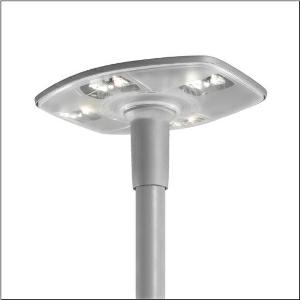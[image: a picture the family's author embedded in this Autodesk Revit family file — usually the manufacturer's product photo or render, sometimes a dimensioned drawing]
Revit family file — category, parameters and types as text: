
# Revit family: dl_30_led___st1_2c_5xa513281b08a5_8ddb
name_source: partatom
category: Lighting Fixtures
units: mm (PartAtom-declared; Revit-internal decimal feet)

## family parameters
Cut with Voids When Loaded = No
Host = Face
Light Source = No
Part Type = Normal
Room Calculation Point = No
Round Connector Dimension = Use Diameter
Shared = No

## types (1)
- --- (1 x LED, 4590 lm, 49 W, 3000K)
    Apparent Load = 49 VA
    CIE Flux Codes = 32 71 98 100 100
    Color Rendering = 80
    Color Temperature = 3000K
    Default Elevation = 1800 mm
    Description = DL 30 LED, mast luminaire, primary light control with 3 zone facetted reflector, of plastic, aluminium vaporised, highly specular, primary optical cover: cover, of PMMA, structured, transparent, light distribution: ST1.2c, light emission: direct distribution, primary light characteristic: asymmetric, crossroads, installation type: post-top, LED, High Power LED, rated luminous flux: 4.590lm, luminous efficacy: 94lm/W, light colour: 830, colour temperature: 3000K, control gear: Plus, control: flexible luminous flux parameterisation, time-dependent luminous flux control, constant luminous flux control, digital communication interface, power reduction, electronic power reduction, mains connection: 230..240V, AC, 50/60Hz, start of lifetime: 49W, end of service life: 51W, reduction: 22W, luminaire housing, of diecast aluminium, powder-coated, SITECO metallic grey (DB 702S), length: 600mm, width: 510mm, height: 290mm, spigot size: d x l = 76 x 100mm (post-top) | with reducer (optional accessory) 60 x 100mm, mounting height: 3..6m, protection rating (complete): IP66, insulation class (complete): insulation class II (safety insulation), certification: CE, ENEC, VDE, impact resistance: IK08, permissible operating ambient temperature: -25..+30°C, standard-compliant lighting for roads and squares, packaging unit: 1 piece

Light Distribution: ST1.2c
    Height = 290 mm
    Lamp = 1 x LED
    Lamp Light Flux = 4590 lm
    Lamp Power = 49 W
    Lamp count = 1
    Length = 510 mm
    Luminous efficacy = 94 lm/W
    Manufacturer = Siteco
    ModVariant = No
    Model = 5XA513281B08A5
    Mounting Place = Pole
    Mounting Type = Pole top
    Number of Poles = 1
    OnlyDefault = Yes
    Power Factor = 1
    Product Name = DL 30 LED | ST1.2c
    Product group = mast luminaire | pylon top
    ProductGroupID = 6100
    Protection Class = Protection class II
    Protection Degree = IP 66
    RLX_Detail_Level = 1
    RLX_Emergency_Light_Flux = 0 lm
    RLX_Emergency_Type = 0
    RLX_Emergency_Type_DB = No
    RlxData = <blob elided: 86557 chars, md5=80c81cf2>
    Socket = socket
    Standby Power = 0 W
    System Light Flux = 4590 lm
    System Power = 49 W
    Type Comments = factory setting: luminous flux: 100 % | dim-lin: 254 | 497 mA
    Type Image = l_1006003.jpg
    URL = http://relux.com
    VarID = @adj_196949
    Voltage = 0 V
    Weight = 0.00 kg
    Width = 600 mm

## geometry (parser evidence)
native form markers: Blend x4, Sweep x11
no freeform markers — native parametric forms only
